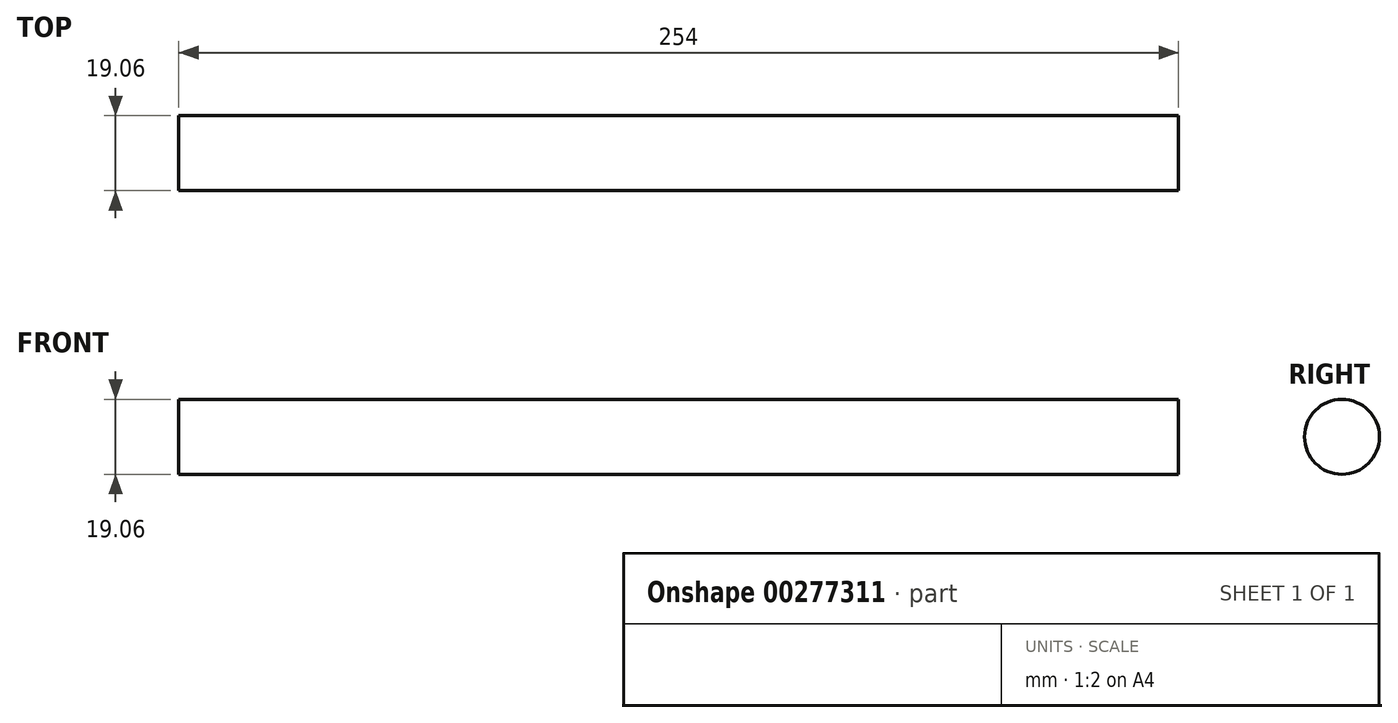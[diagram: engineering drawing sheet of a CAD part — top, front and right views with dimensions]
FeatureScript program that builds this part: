
annotation { "Feature Type Name" : "Feature", "Feature Type Description" : "" }
export const myFeature = defineFeature(function(context is Context, id is Id, definition is map)
    precondition{}
    {
        {
            var Q0;
            Q0=qCreatedBy(makeId("Right.planeOp"),FACE);
            var sketch = newSketch(context, id + "F0", { "sketchPlane" : qUnion([Q0])});
            skCircle(sketch, "E0", {"center": v(0, 0) * mm, "radius": 9.52 * mm});
            skSolve(sketch);
        }
        {
            var Q0;
            Q0 = qSketchRegion(id + "F0", true);
            extrude(context, id + "F1", {"entities" : qUnion([Q0]), "endBound" : BoundingType.SYMMETRIC, "depth" : 254 * mm});
        }
    });
